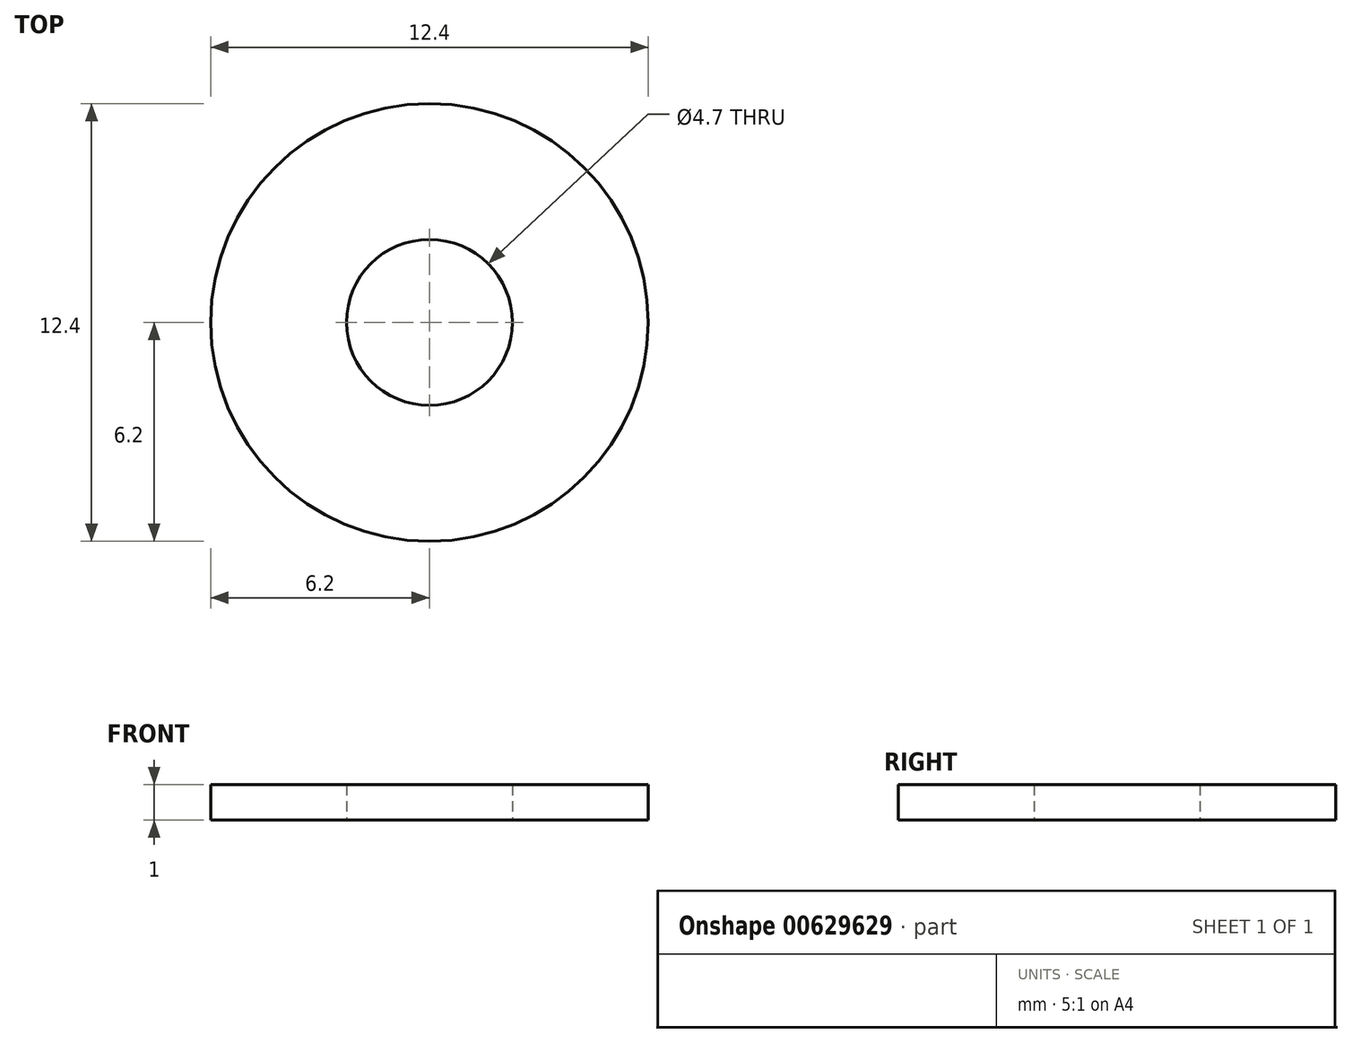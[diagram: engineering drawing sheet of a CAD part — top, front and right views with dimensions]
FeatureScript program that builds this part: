
annotation { "Feature Type Name" : "Feature", "Feature Type Description" : "" }
export const myFeature = defineFeature(function(context is Context, id is Id, definition is map)
    precondition{}
    {
        {
            var Q0;
            Q0=qCreatedBy(makeId("Top.planeOp"),FACE);
            var sketch = newSketch(context, id + "F0", { "sketchPlane" : qUnion([Q0])});
            skCircle(sketch, "E0", {"center": v(0, 0) * mm, "radius": 6.2 * mm});
            skCircle(sketch, "E1", {"center": v(0, 0) * mm, "radius": 2.35 * mm});
            skSolve(sketch);
        }
        {
            var Q0;
            Q0 = qSketchRegion(id + "F0", true);
            extrude(context, id + "F1", {"entities" : qUnion([Q0]), "depth" : 1 * mm, "offsetDistance" : 25 * mm});
        }
    });
